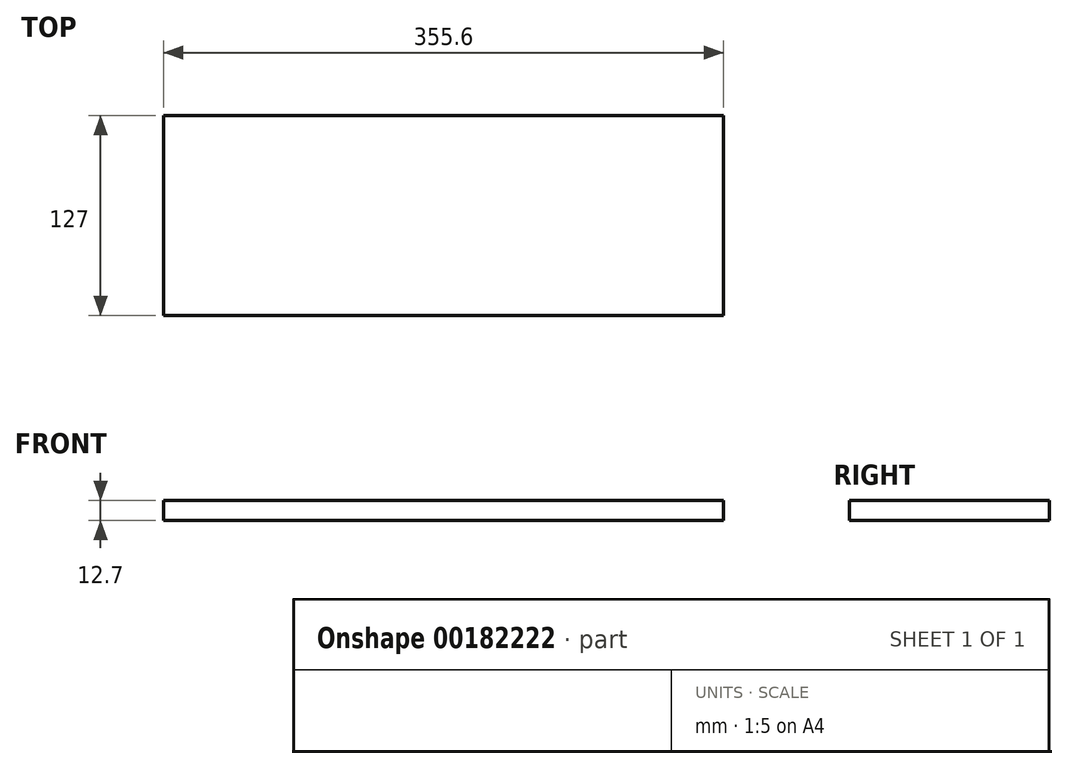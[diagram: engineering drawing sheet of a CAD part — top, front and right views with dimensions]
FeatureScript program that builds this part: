
annotation { "Feature Type Name" : "Feature", "Feature Type Description" : "" }
export const myFeature = defineFeature(function(context is Context, id is Id, definition is map)
    precondition{}
    {
        {
            var Q0;
            Q0=qCreatedBy(makeId("Top.planeOp"),FACE);
            var sketch = newSketch(context, id + "F0", { "sketchPlane" : qUnion([Q0])});
            skLineSegment(sketch, "E0.bottom", {"start": v(0, 0) * mm, "end": v(355.6, 0) * mm});
            skLineSegment(sketch, "E0.top", {"start": v(0, 127) * mm, "end": v(355.6, 127) * mm});
            skLineSegment(sketch, "E0.left", {"start": v(0, 0) * mm, "end": v(0, 127) * mm});
            skLineSegment(sketch, "E0.right", {"start": v(355.6, 0) * mm, "end": v(355.6, 127) * mm});
            skSolve(sketch);
        }
        {
            var Q0;
            Q0=makeQuery(id+"F0.imprint","IMPRINT",FACE,{"disambiguationData":[TD([[makeQuery(id+"F0.imprint","IMPRINT",EDGE,{"derivedFrom":sQuery(id+"F0.wireOp",EDGE,"E0.bottom")}),1.0]])]});
            extrude(context, id + "F1", {"entities" : qUnion([Q0]), "depth" : 12.7 * mm});
        }
    });
